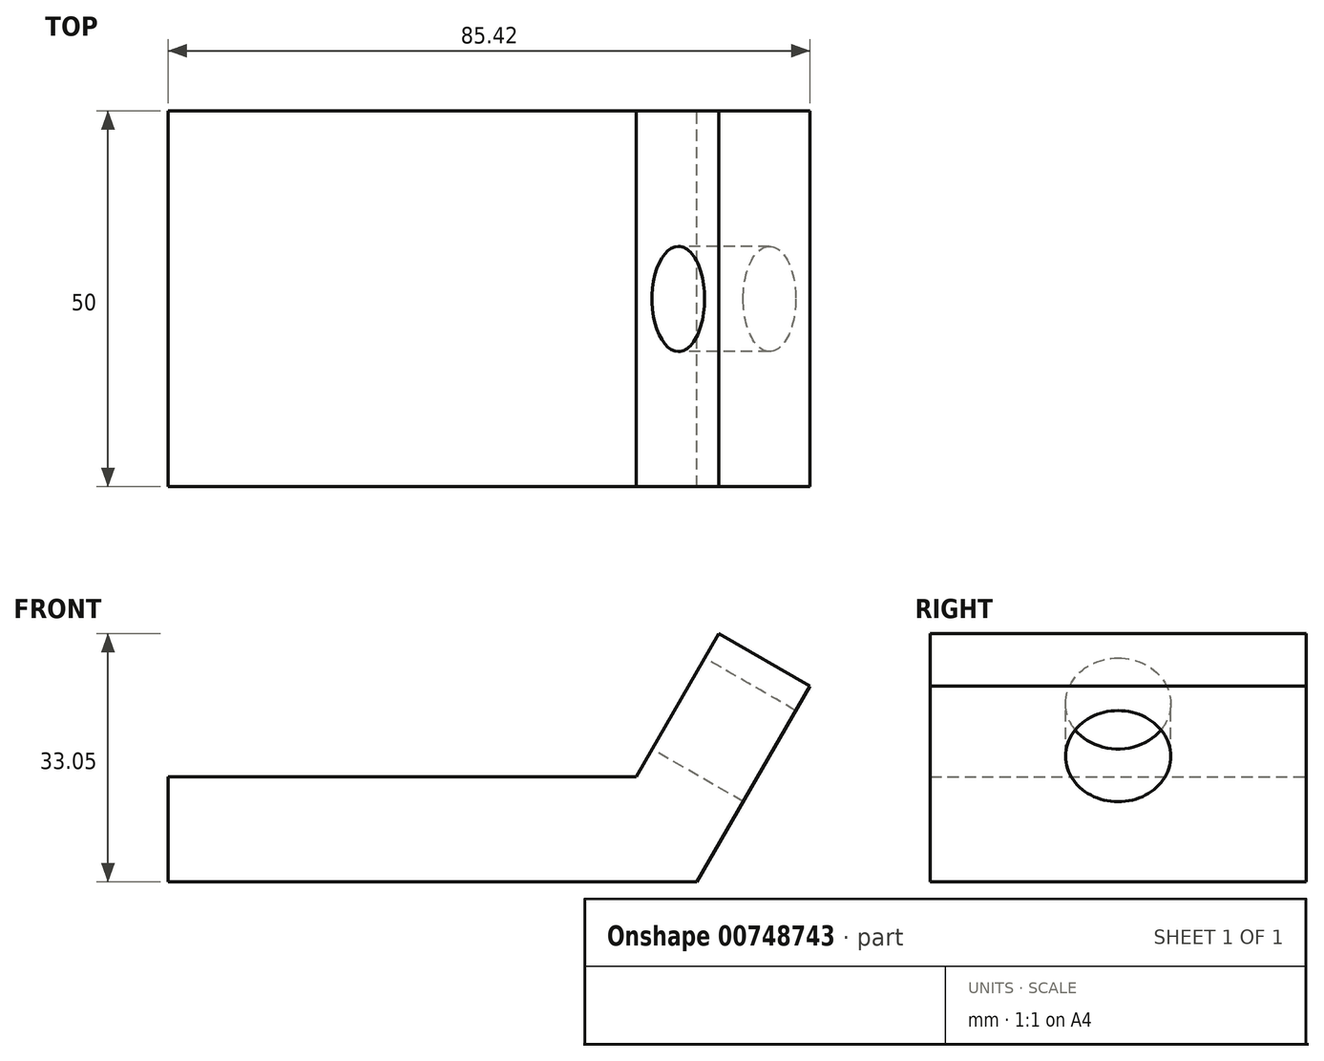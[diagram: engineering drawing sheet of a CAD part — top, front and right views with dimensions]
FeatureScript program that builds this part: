
annotation { "Feature Type Name" : "Feature", "Feature Type Description" : "" }
export const myFeature = defineFeature(function(context is Context, id is Id, definition is map)
    precondition{}
    {
        {
            var Q0;
            Q0=qCreatedBy(makeId("Front.planeOp"),FACE);
            var sketch = newSketch(context, id + "F0", { "sketchPlane" : qUnion([Q0])});
            skLineSegment(sketch, "E0", {"start": v(-47.5, 14.57) * mm, "end": v(14.8, 14.57) * mm});
            skLineSegment(sketch, "E1", {"start": v(14.8, 14.57) * mm, "end": v(25.8, 33.62) * mm});
            skLineSegment(sketch, "E2", {"start": v(25.8, 33.62) * mm, "end": v(37.92, 26.62) * mm});
            skLineSegment(sketch, "E3", {"start": v(37.92, 26.62) * mm, "end": v(22.88, 0.57) * mm});
            skLineSegment(sketch, "E4", {"start": v(22.88, 0.57) * mm, "end": v(-47.5, 0.57) * mm});
            skLineSegment(sketch, "E5", {"start": v(-47.5, 0.57) * mm, "end": v(-47.5, 14.57) * mm});
            skSolve(sketch);
        }
        {
            var Q0;
            Q0=makeQuery(id+"F0.imprint","IMPRINT",FACE,{"disambiguationData":[TD([[makeQuery(id+"F0.imprint","IMPRINT",EDGE,{"derivedFrom":sQuery(id+"F0.wireOp",EDGE,"E0")}),-1.0]])]});
            extrude(context, id + "F1", {"entities" : qUnion([Q0]), "depth" : 50 * mm});
        }
        {
            var Q0;
            Q0=makeQuery(id+"F1.opExtrude","SWEPT_FACE",FACE,{"disambiguationData":[OSD([sQuery(id+"F0.wireOp",EDGE,"E1")])]});
            var sketch = newSketch(context, id + "F2", { "sketchPlane" : qUnion([Q0])});
            skCircle(sketch, "E6", {"center": v(25, 31.23) * mm, "radius": 7 * mm});
            skSolve(sketch);
        }
        {
            var Q0;
            Q0=qSketchRegion(id+"F2",true);
            extrude(context, id + "F3", {"entities" : qUnion([Q0]), "operationType" : NewBodyOperationType.REMOVE, "endBound" : BoundingType.THROUGH_ALL, "oppositeDirection" : true, "depth" : 25 * mm});
        }
    });
